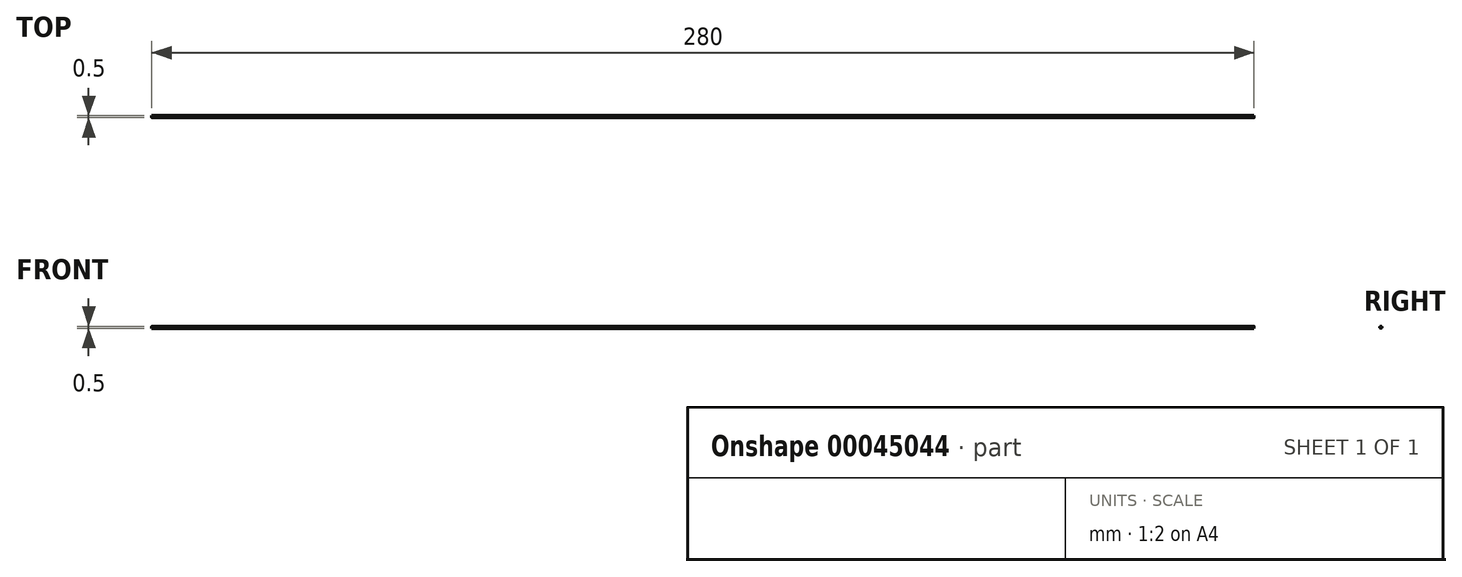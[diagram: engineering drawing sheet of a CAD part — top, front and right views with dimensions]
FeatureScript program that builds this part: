
annotation { "Feature Type Name" : "Feature", "Feature Type Description" : "" }
export const myFeature = defineFeature(function(context is Context, id is Id, definition is map)
    precondition{}
    {
        {
            var Q0;
            Q0=qCreatedBy(makeId("Right.planeOp"),FACE);
            var sketch = newSketch(context, id + "F0", { "sketchPlane" : qUnion([Q0])});
            skCircle(sketch, "E0", {"center": v(0, 0) * mm, "radius": 0.25 * mm});
            skSolve(sketch);
        }
        {
            var Q0;
            Q0 = qSketchRegion(id + "F0", true);
            extrude(context, id + "F1", {"entities" : qUnion([Q0]), "depth" : 280 * mm});
        }
    });
